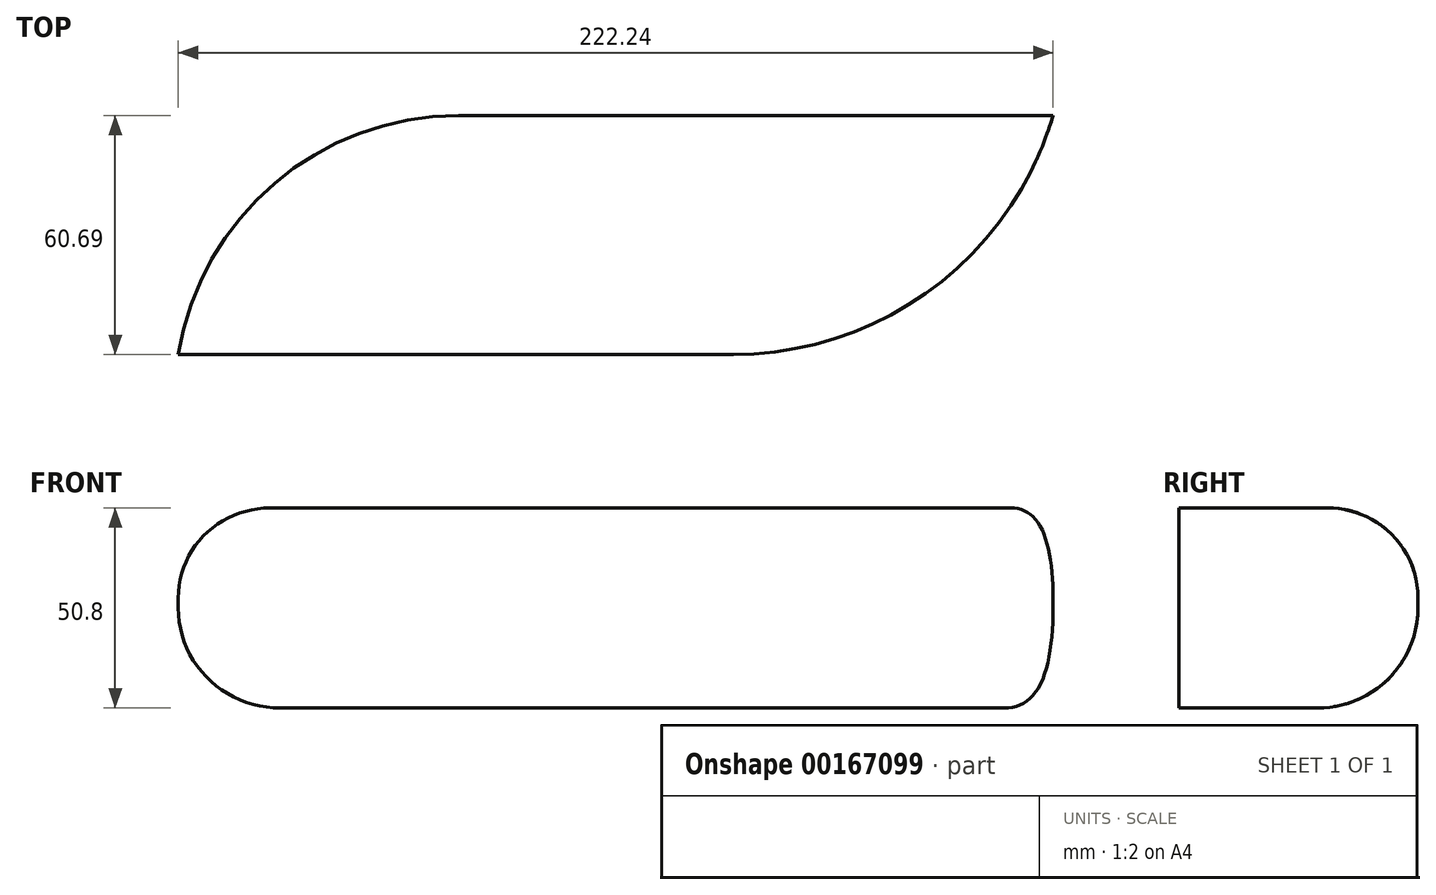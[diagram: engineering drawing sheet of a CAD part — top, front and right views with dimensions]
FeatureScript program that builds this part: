
annotation { "Feature Type Name" : "Feature", "Feature Type Description" : "" }
export const myFeature = defineFeature(function(context is Context, id is Id, definition is map)
    precondition{}
    {
        {
            var Q0;
            Q0=qCreatedBy(makeId("Top.planeOp"),FACE);
            var sketch = newSketch(context, id + "F0", { "sketchPlane" : qUnion([Q0])});
            skLineSegment(sketch, "E0", {"start": v(-57.76, 60.72) * mm, "end": v(83.25, 60.72) * mm});
            skArc(sketch, "E1", {"start": v(83.25, 60.72) * mm, "mid": v(133.95, 77.57) * mm, "end": v(164.48, 121.41) * mm});
            skLineSegment(sketch, "E2", {"start": v(164.48, 121.41) * mm, "end": v(13.43, 121.41) * mm});
            skArc(sketch, "E3", {"start": v(13.43, 121.41) * mm, "mid": v(-33.35, 104.18) * mm, "end": v(-57.76, 60.72) * mm});
            skSolve(sketch);
        }
        {
            var Q0;
            Q0=qSketchRegion(id+"F0",true);
            extrude(context, id + "F1", {"entities" : qUnion([Q0]), "depth" : 50.8 * mm});
        }
        {
            var Q0;
            Q0=makeQuery(id+"F1.opExtrude","CAP_EDGE",EDGE,{"disambiguationData":[OSD([sQuery(id+"F0.wireOp",EDGE,"E3")])],"isStart":false});
            var Q1;
            Q1=makeQuery(id+"F1.opExtrude","CAP_EDGE",EDGE,{"disambiguationData":[OSD([sQuery(id+"F0.wireOp",EDGE,"E2")])],"isStart":false});
            fillet(context, id + "F2", {"entities" : qUnion([Q0, Q1]), "radius" : 22.86 * mm, "tangentPropagation" : true, "allowEdgeOverflow" : false});
        }
        {
            var Q0;
            Q0=makeQuery(id+"F1.opExtrude","CAP_EDGE",EDGE,{"disambiguationData":[OSD([sQuery(id+"F0.wireOp",EDGE,"E2")])],"isStart":true});
            var Q1;
            Q1=makeQuery(id+"F1.opExtrude","CAP_EDGE",EDGE,{"disambiguationData":[OSD([sQuery(id+"F0.wireOp",EDGE,"E3")])],"isStart":true});
            fillet(context, id + "F3", {"entities" : qUnion([Q0, Q1]), "radius" : 25.4 * mm, "tangentPropagation" : true, "allowEdgeOverflow" : false});
        }
    });
